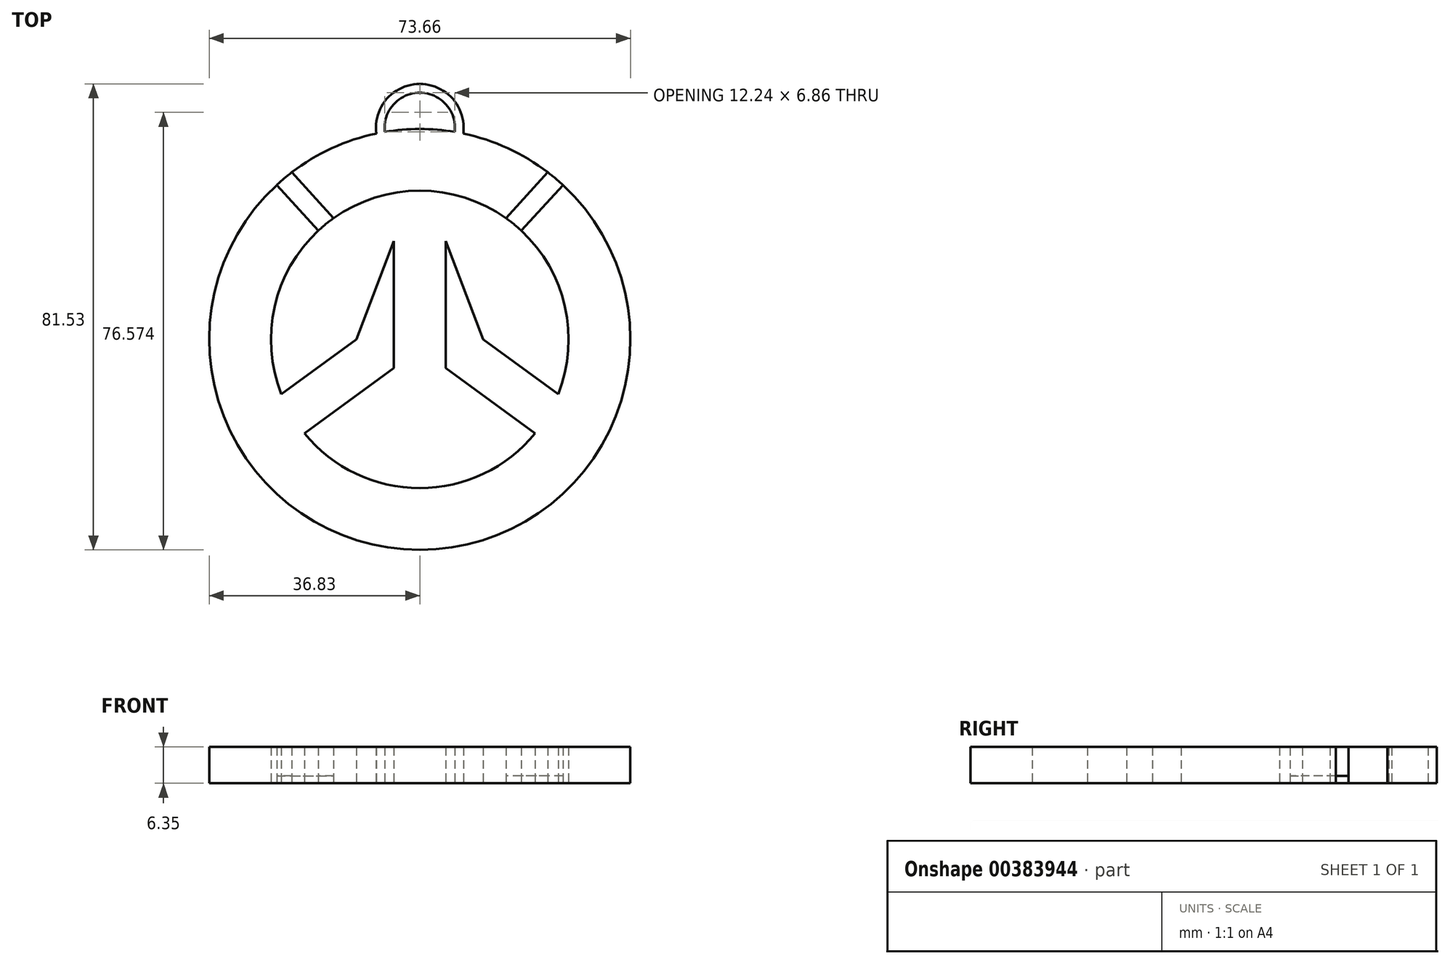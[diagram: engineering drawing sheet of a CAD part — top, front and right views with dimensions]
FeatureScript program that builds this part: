
annotation { "Feature Type Name" : "Feature", "Feature Type Description" : "" }
export const myFeature = defineFeature(function(context is Context, id is Id, definition is map)
    precondition{}
    {
        {
            var Q0;
            Q0=qCreatedBy(makeId("Top.planeOp"),FACE);
            var sketch = newSketch(context, id + "F0", { "sketchPlane" : qUnion([Q0])});
            skCircle(sketch, "E0", {"center": v(0, 0) * mm, "radius": 36.83 * mm});
            skLineSegment(sketch, "E1", {"start": v(0, 0) * mm, "end": v(0, 0) * mm});
            skLineSegment(sketch, "E2", {"start": v(36.83, 0) * mm, "end": v(36.83, 0) * mm});
            skArc(sketch, "E3", {"start": v(-20.18, -16.43) * mm, "mid": v(0, -26.02) * mm, "end": v(20.18, -16.43) * mm});
            skLineSegment(sketch, "E4", {"start": v(-4.51, 0) * mm, "end": v(-4.51, -5.04) * mm});
            skLineSegment(sketch, "E5", {"start": v(-4.51, 17.22) * mm, "end": v(-4.51, -5.04) * mm});
            skLineSegment(sketch, "E6", {"start": v(4.51, 17.39) * mm, "end": v(4.51, 17.39) * mm});
            skLineSegment(sketch, "E7", {"start": v(-4.51, -5.04) * mm, "end": v(-20.18, -16.43) * mm});
            skLineSegment(sketch, "E8.MirrorCS", {"start": v(4.51, -5.04) * mm, "end": v(4.51, -5.04) * mm});
            skLineSegment(sketch, "E9", {"start": v(-4.51, -5.04) * mm, "end": v(-4.51, 17.39) * mm});
            skLineSegment(sketch, "E10", {"start": v(4.51, -5.04) * mm, "end": v(20.18, -16.43) * mm});
            skLineSegment(sketch, "E11", {"start": v(4.51, -5.04) * mm, "end": v(4.51, 17.39) * mm});
            skLineSegment(sketch, "E12", {"start": v(-17, -4.33) * mm, "end": v(-24.2, -9.56) * mm});
            skLineSegment(sketch, "E13", {"start": v(-4.51, 17.22) * mm, "end": v(-11.05, 0) * mm});
            skLineSegment(sketch, "E14", {"start": v(-11.05, 0) * mm, "end": v(-17, -4.33) * mm});
            skLineSegment(sketch, "E15.MirrorCS", {"start": v(4.51, 17.22) * mm, "end": v(11.05, 0) * mm});
            skLineSegment(sketch, "E16.MirrorCS", {"start": v(11.05, 0) * mm, "end": v(17, -4.33) * mm});
            skLineSegment(sketch, "E17.MirrorCS", {"start": v(17, -4.33) * mm, "end": v(24.2, -9.56) * mm});
            skLineSegment(sketch, "E18", {"start": v(-24.2, -9.56) * mm, "end": v(-24.2, -9.56) * mm});
            skArc(sketch, "E19.trimOffspring", {"start": v(24.2, -9.56) * mm, "mid": v(25.38, 5.73) * mm, "end": v(17.75, 19.03) * mm});
            skLineSegment(sketch, "E20", {"start": v(-25.02, 27.02) * mm, "end": v(-17.75, 19.03) * mm});
            skLineSegment(sketch, "E21", {"start": v(-22.38, 29.25) * mm, "end": v(-15.07, 21.21) * mm});
            skArc(sketch, "E22.trimOffspring", {"start": v(-17.75, 19.03) * mm, "mid": v(-25.38, 5.73) * mm, "end": v(-24.2, -9.56) * mm});
            skLineSegment(sketch, "E23.MirrorCS", {"start": v(22.38, 29.25) * mm, "end": v(15.07, 21.21) * mm});
            skLineSegment(sketch, "E24.MirrorCS", {"start": v(25.02, 27.02) * mm, "end": v(17.75, 19.03) * mm});
            skArc(sketch, "E25.trimOffspring", {"start": v(15.07, 21.21) * mm, "mid": v(0, 26.02) * mm, "end": v(-15.07, 21.21) * mm});
            skArc(sketch, "E26", {"start": v(-8.39, 24.63) * mm, "mid": v(-15.44, 20.95) * mm, "end": v(-21.05, 15.3) * mm});
            skArc(sketch, "E27.MirrorCS", {"start": v(8.39, 24.63) * mm, "mid": v(15.44, 20.95) * mm, "end": v(21.05, 15.3) * mm});
            skArc(sketch, "E28", {"start": v(7.62, 36.03) * mm, "mid": v(0, 44.7) * mm, "end": v(-7.62, 36.03) * mm});
            skArc(sketch, "E29", {"start": v(0, 43.18) * mm, "mid": v(4.6, 41.12) * mm, "end": v(6.12, 36.31) * mm});
            skArc(sketch, "E30.MirrorCS", {"start": v(0, 43.18) * mm, "mid": v(-4.6, 41.12) * mm, "end": v(-6.12, 36.31) * mm});
            skLineSegment(sketch, "E31", {"start": v(-7.62, 36.03) * mm, "end": v(-7.62, 36.03) * mm});
            skSolve(sketch);
        }
        {
            var Q0;
            {var subQ2=sQuery(id+"F0.wireOp",EDGE,"E21");Q0=makeQuery(id+"F0.imprint","IMPRINT",FACE,{"disambiguationData":[TD([[makeQuery(id+"F0.imprint","IMPRINT",EDGE,{"derivedFrom":subQ2}),1.0]])]});}
            extrude(context, id + "F1", {"entities" : qUnion([Q0]), "depth" : 6.35 * mm});
        }
        {
            var Q0;
            Q0=makeQuery(id+"F0.imprint","IMPRINT",FACE,{"disambiguationData":[TD([[makeQuery(id+"F0.imprint","IMPRINT",EDGE,{"derivedFrom":sQuery(id+"F0.wireOp",EDGE,"E3")}),-1.0]])]});
            extrude(context, id + "F2", {"entities" : qUnion([Q0]), "depth" : 6.35 * mm});
        }
        {
            var Q0;
            {var subQ0=sQuery(id+"F0.wireOp",EDGE,"E20");Q0=makeQuery(id+"F0.imprint","IMPRINT",FACE,{"disambiguationData":[TD([[makeQuery(id+"F0.imprint","IMPRINT",EDGE,{"derivedFrom":subQ0}),1.0]])]});}
            extrude(context, id + "F3", {"entities" : qUnion([Q0]), "depth" : 1.27 * mm});
        }
        {
            var Q0;
            {var subQ0=sQuery(id+"F0.wireOp",EDGE,"E23.MirrorCS");Q0=makeQuery(id+"F0.imprint","IMPRINT",FACE,{"disambiguationData":[TD([[makeQuery(id+"F0.imprint","IMPRINT",EDGE,{"derivedFrom":subQ0}),1.0]])]});}
            extrude(context, id + "F4", {"entities" : qUnion([Q0]), "depth" : 1.27 * mm});
        }
        {
            var Q0;
            {var subQ0=sQuery(id+"F0.wireOp",EDGE,"E29");Q0=makeQuery(id+"F0.imprint","IMPRINT",FACE,{"disambiguationData":[TD([[makeQuery(id+"F0.imprint","IMPRINT",EDGE,{"derivedFrom":subQ0}),-1.0]])]});}
            extrude(context, id + "F5", {"entities" : qUnion([Q0]), "operationType" : NewBodyOperationType.REMOVE, "oppositeDirection" : true, "depth" : 6.35 * mm});
        }
        {
            var Q0;
            {var subQ0=sQuery(id+"F0.wireOp",EDGE,"E28");Q0=makeQuery(id+"F0.imprint","IMPRINT",FACE,{"disambiguationData":[TD([[makeQuery(id+"F0.imprint","IMPRINT",EDGE,{"derivedFrom":subQ0}),1.0]])]});}
            extrude(context, id + "F6", {"entities" : qUnion([Q0]), "operationType" : NewBodyOperationType.ADD, "depth" : 6.35 * mm});
        }
    });
